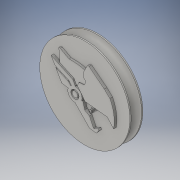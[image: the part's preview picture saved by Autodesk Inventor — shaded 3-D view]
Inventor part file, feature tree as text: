
AUTODESK INVENTOR PART (.ipt)
format: ipt  version: 2016 (Build 200138000, 138)  size: 336,896 bytes
history: native  units: in
note: dims shown in document units (in); Inventor stores cm internally (conversion verified against a paired STEP export)
features: extrude x4, sketch x4, revolve x1, other x1
ambient origin geometry x8: Origin, YZ Plane, XZ Plane, XY Plane, X Axis, Y Axis, Z Axis, Center Point
bodies: Solid1 (feature_tree)
feature tree (10):
  extrude  "Extrusion1"  Depth=0.25in TaperAngle=0.0deg
  revolve  "Revolution1"  Angle=90.0deg
  extrude  "Extrusion3"  Depth=0.192in
  sketch  "Sketch7"  dims[d45=0.14in d46=0.2038in d47=0.096in d102=0.04in d103=0.0in d105=0.05in d106=0.0in]
  extrude  "Extrusion5"  Depth=0.05in
  extrude  "Extrusion6"  Depth=0.05in
  sketch  "Sketch1"  dims[d0=1.73in d1=0.25in d2=0.0in]
  sketch  "Sketch3"  dims[d37=0.2in d38=90.0deg]
  sketch  "Sketch4"  dims[d42=0.206in d43=0.0in d44=0.192in]
  other  "Image3"
